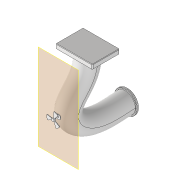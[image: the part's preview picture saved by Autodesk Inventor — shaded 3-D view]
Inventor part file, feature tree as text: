
AUTODESK INVENTOR PART (.ipt)
format: ipt  version: 2020 (Build 240168000, 168)  size: 731,136 bytes
history: native  units: mm
features: sketch x9, extrude x6, chamfer x3, fillet x2, sweep x1, plane x1, revolve x1, pattern_circular x1
ambient origin geometry x8: Origin, YZ Plane, XZ Plane, XY Plane, X Axis, Y Axis, Z Axis, Center Point
bodies: Volumenkörper1 (feature_tree)
feature tree (24):
  sweep  "Sweeping1"
  extrude  "Extrusion1"  Depth=10.0mm TaperAngle=0.0deg
  extrude  "Extrusion2"  Depth=300.0mm
  chamfer  "Fase1"  Distance=50.0mm
  chamfer  "Fase2"  Distance=5.0mm Angle=45.0deg
  fillet  "Rundung1"  Radius=2.0mm
  plane  "Arbeitsebene1"
  extrude  "Extrusion3"  Depth=4.769mm TaperAngle=0.0deg
  extrude  "Extrusion4"  Depth=40.0mm TaperAngle=0.0deg
  extrude  "Extrusion5"  Depth=20.0mm TaperAngle=0.0deg
  revolve  "Umdrehung1"
  fillet  "Rundung2"  Radius=60.0mm
  pattern_circular  "Runde Anordnung1"  [2 undecoded]
  extrude  "Extrusion6"  Depth=20.0mm
  chamfer  "Fase3"  Distance=30.0mm Angle=360.0deg
  sketch  "Skizze1"  dims[d0=200.0mm d1=220.0mm]
  sketch  "Skizze2"  dims[d2=0.0mm d3=0.0mm d4=10.0mm d5=0.0mm]
  sketch  "Skizze3"  dims[d6=400.0mm d7=300.0mm d8=50.0mm d9=0.0mm d10=5.0mm d11=2.0mm d12=45.0deg]
  sketch  "Skizze4"  dims[d13=10.0mm d14=2.0mm d15=45.0deg d16=2.0mm]
  sketch  "Skizze5"  dims[d17=50.0mm d18=4.769mm d19=0.0mm]
  sketch  "Skizze6"  dims[d20=15.0mm d21=40.0mm d22=0.0mm]
  sketch  "Skizze7"  dims[d23=30.0mm d24=20.0mm d25=0.0mm d26=60.0mm]
  sketch  "Skizze8"  dims[d27=5.0mm]
  sketch  "Skizze9"  dims[d28=5.0mm d29=6.981317mm d30=5.0mm d31=30.0mm d32=360.0deg d34=250.0mm d35=20.0mm d36=0.0mm d37=4.0mm d38=2.0mm d39=45.0deg]
note: 2 required parameter values undecoded (feature->parameter linkage not recoverable at this tier; creation-order binding heuristic only, values carry confidence <= 0.55)
